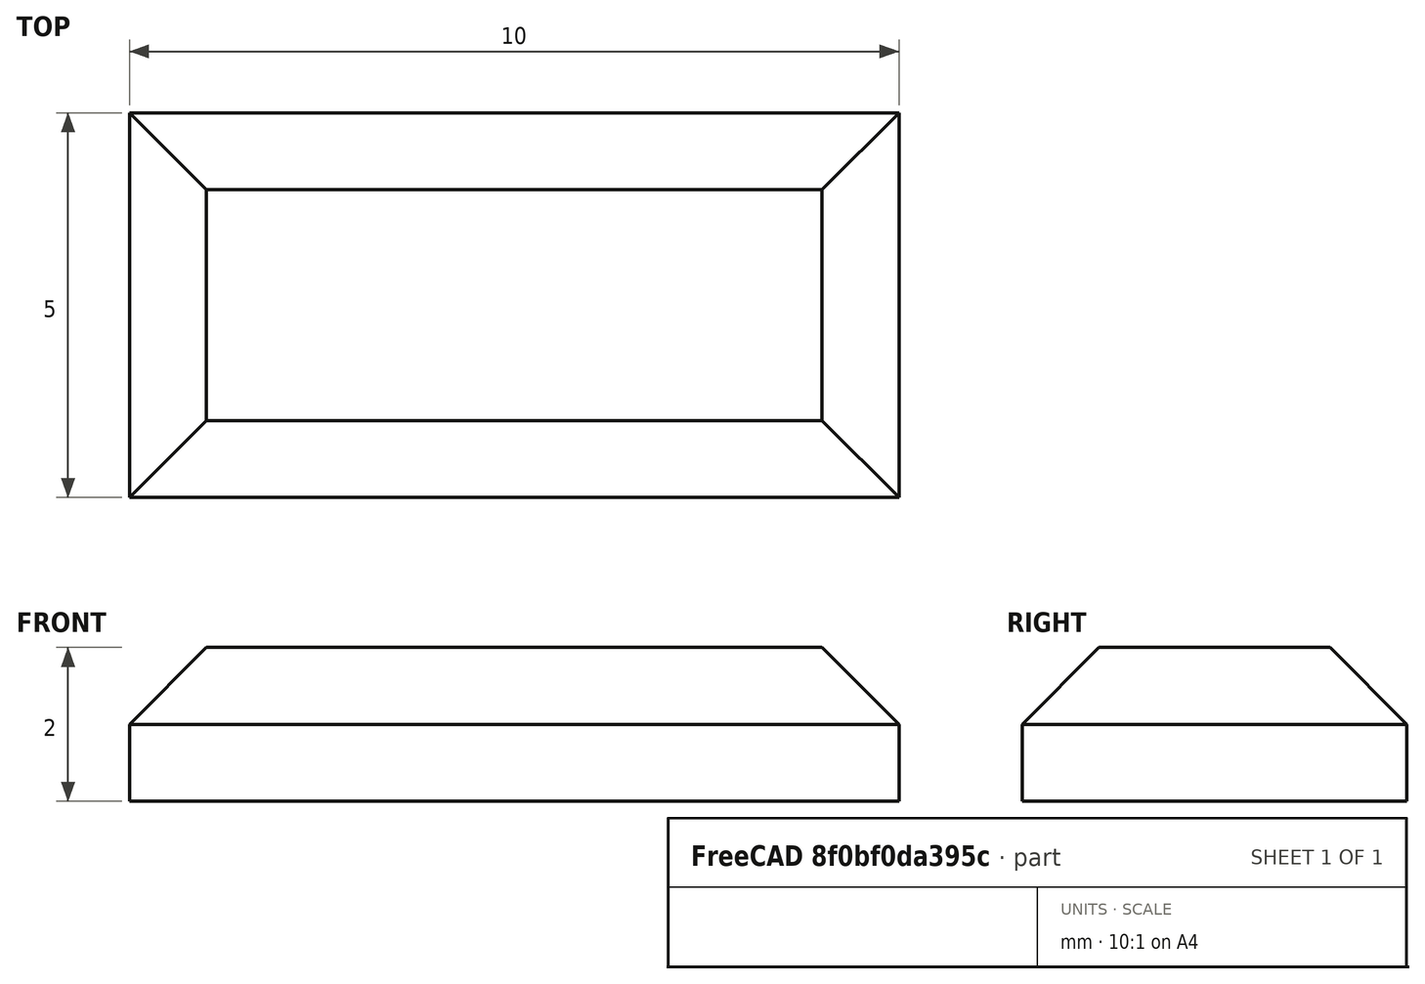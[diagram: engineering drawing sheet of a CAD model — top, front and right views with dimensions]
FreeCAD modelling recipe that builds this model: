
FCSTD DOCUMENT  (FreeCAD 0.21R33694 (Git))
Label: OJT1_T12R02_chocolate
License: All rights reserved
LicenseURL: http://en.wikipedia.org/wiki/All_rights_reserved
objects: Part::Box×1, Part::Chamfer×1, Part::FeaturePython×1
note: 2 computed .brp shape members not serialized (recipe doc carries the construction recipe); baked Part::Feature solids carry a one-line shape summary decoded from their .brp

FEATURE [Part::Box] Box  label="Cube"
  AttacherType = Attacher::AttachEngine3D
  Height = 2
  Length = 10
  Width = 5
FEATURE [Part::Chamfer] Chamfer
  Base = -> Box
  Edges = 4 edges r=1: [Edge2,Edge6,Edge10,Edge12]
FEATURE [Part::FeaturePython] Array  # Draft array (typed FeaturePython)
  AlwaysSyncPlacement = false
  Angle = 360
  ArrayType = 0
  Axis = (0,0,1)
  Base = -> Chamfer
  Center = (0,0,0)
  Count = 16
  ExpandArray = false
  Fuse = false
  IntervalAxis = (0,0,0)
  IntervalX = (10,0,0)
  IntervalY = (0,5,0)
  IntervalZ = (0,0,100)
  NumberCircles = 3
  NumberPolar = 5
  NumberX = 4
  NumberY = 4
  NumberZ = 1
  PlacementList = 16 placements: [(0,0,0),(0,5,0),(0,10,0),(0,15,0),(10,0,0),(10,5,0),(10,10,0),(10,15,0),(20,0,0),(20,5,0),(20,10,0),(20,15,0),(30,0,0),(30,5,0),(30,10,0),(30,15,0)]
  RadialDistance = 50
  ScaleList = (16) [(1,1,1),(1,1,1),(1,1,1),(1,1,1),(1,1,1),(1,1,1),(1,1,1),(1,1,1),(1,1,1),(1,1,1),(1,1,1),(1,1,1),(1,1,1),(1,1,1),(1,1,1),(1,1,1)]
  Symmetry = 1
  TangentialDistance = 25
